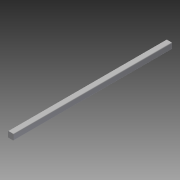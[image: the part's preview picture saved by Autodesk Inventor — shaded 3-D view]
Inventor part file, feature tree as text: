
AUTODESK INVENTOR PART (.ipt)
format: ipt  version: 2014 SP1 (Build 180222100, 222)  size: 82,944 bytes
history: native  units: in
note: dims shown in document units (in); Inventor stores cm internally (conversion verified against a paired STEP export)
features: plane x2, extrude x1, fillet x1, other x1, sketch x1
ambient origin geometry x8: Origin, YZ Plane, XZ Plane, XY Plane, X Axis, Y Axis, Z Axis, Center Point
bodies: Solid1 (feature_tree)
feature tree (6):
  extrude  "Extrusion1"  Depth=0.127in
  fillet  "Fillet1"  Radius=3.5in
  other  "Work Axis1"
  sketch  "Sketch1"  dims[d0=0.127in d1=0.127in d2=3.5in d3=0.0in d4=0.015in]
  plane  "Work Plane1"
  plane  "Work Plane2"
